# Revit family: 206_FSBQL-_
name_source: partatom
category: Duct Accessories
units: mm (PartAtom-declared; Revit-internal decimal feet)

## family parameters
Always vertical = Yes
Cut with Voids When Loaded = No
Part Type = Breaks Into
Round Connector Dimension = Use Diameter
Shared = No
Work Plane-Based = No

## types (11) — shared parameters
CAT0 = Yes
Description = FILTER BOX
L2D = 160 mm  [stored 0.524934 ft]
LL = 80 mm  [stored 0.262467 ft]
Manufacturer = Alnor
QmdConnectorList = 201;D;202;D
URL = http://www.ventilation-alnor.co.uk
magiPartTypeId = 206
magiProductFamilyId = FSBQL-*

## per-type parameters (varying)
| type | CBB | CH | CHH | D | H2D | W2D |
| FSBQL-100 | 80 mm  [stored 0.262467 ft] | 160 mm  [stored 0.524934 ft] | 80 mm  [stored 0.262467 ft] | 100 mm | 100 mm  [stored 0.328084 ft] | 100 mm  [stored 0.328084 ft] |
| FSBQL-500 | 275 mm | 550 mm | 275 mm | 500 mm | 500 mm | 500 mm |
| FSBQL-450 | 250 mm | 500 mm | 250 mm | 450 mm | 450 mm | 450 mm |
| FSBQL-400 | 225 mm | 450 mm | 225 mm | 400 mm | 400 mm | 400 mm |
| FSBQL-355 | 200 mm | 400 mm | 200 mm | 355 mm | 355 mm | 355 mm |
| FSBQL-315 | 180 mm | 360 mm | 180 mm | 315 mm | 315 mm | 315 mm |
| FSBQL-250 | 150 mm | 300 mm | 150 mm | 250 mm | 250 mm | 250 mm |
| FSBQL-200 | 125 mm | 250 mm | 125 mm | 200 mm | 200 mm | 200 mm |
| FSBQL-160 | 105 mm | 210 mm | 105 mm | 160 mm | 160 mm  [stored 0.524934 ft] | 160 mm  [stored 0.524934 ft] |
| FSBQL-150 | 105 mm | 210 mm | 105 mm | 150 mm | 150 mm | 150 mm |
| FSBQL-125 | 90 mm | 180 mm | 90 mm | 125 mm | 125 mm | 125 mm |

note: column(s) folded — value = type name in every type: MC Product Code, magiProductId

note: [stored X ft] marks values corroborated as IEEE doubles in the binary element streams (Revit-internal decimal feet)

## geometry (parser evidence)
native form markers: Blend x4, Sweep x2
no freeform markers — native parametric forms only
